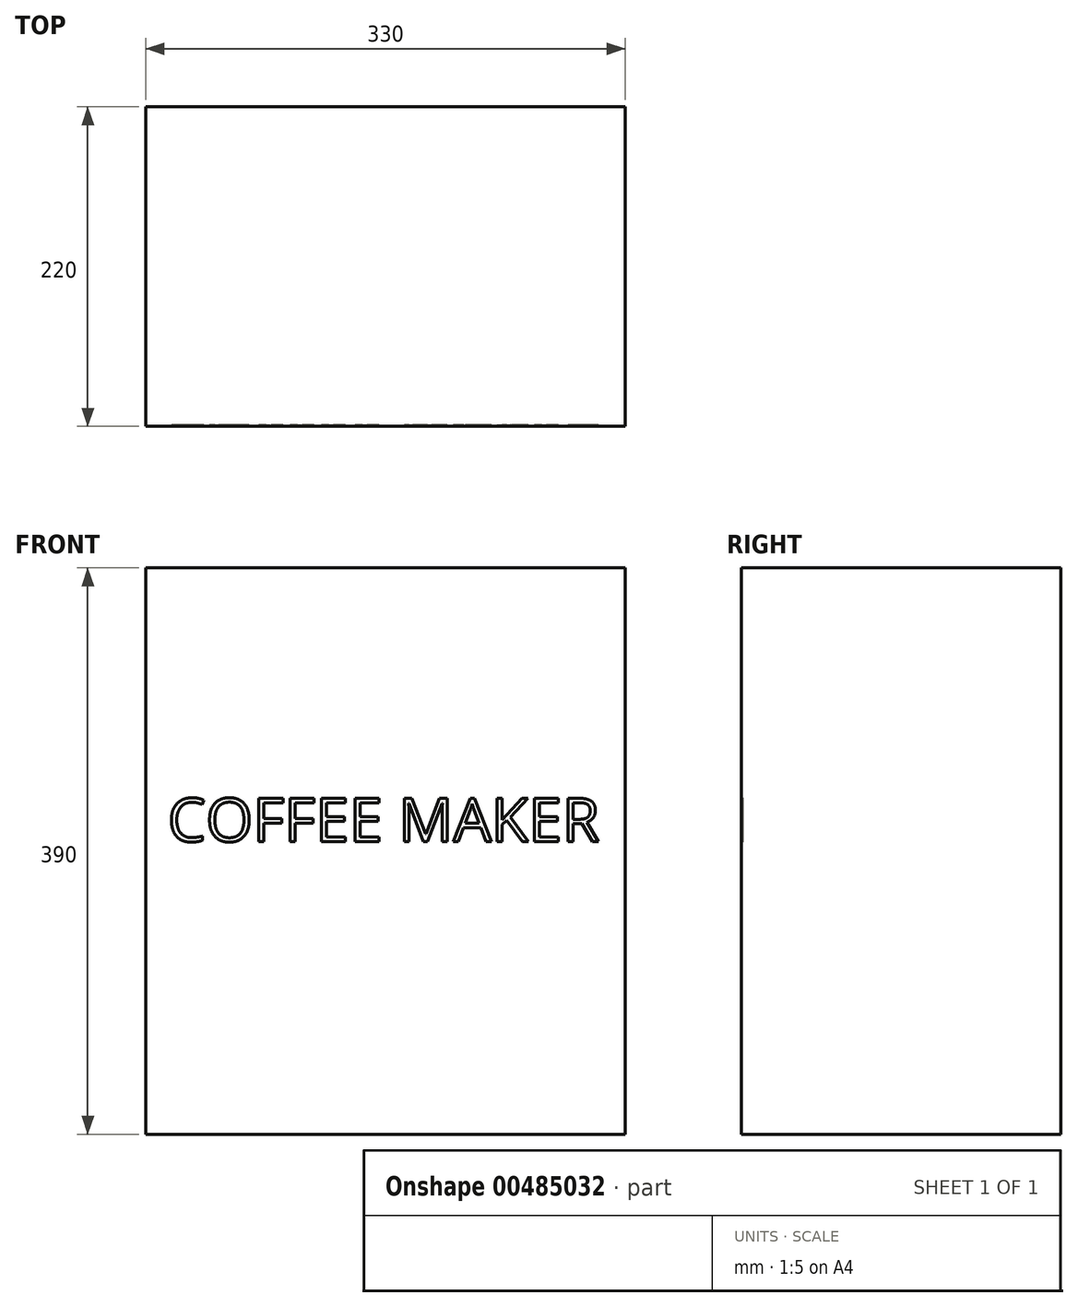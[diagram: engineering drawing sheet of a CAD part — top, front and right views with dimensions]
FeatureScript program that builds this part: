
annotation { "Feature Type Name" : "Feature", "Feature Type Description" : "" }
export const myFeature = defineFeature(function(context is Context, id is Id, definition is map)
    precondition{}
    {
        {
            var Q0;
            Q0=qCreatedBy(makeId("Top.planeOp"),FACE);
            var sketch = newSketch(context, id + "F0", { "sketchPlane" : qUnion([Q0])});
            skLineSegment(sketch, "E0.bottom", {"start": v(165, -110) * mm, "end": v(-165, -110) * mm});
            skLineSegment(sketch, "E0.top", {"start": v(165, 110) * mm, "end": v(-165, 110) * mm});
            skLineSegment(sketch, "E0.left", {"start": v(165, -110) * mm, "end": v(165, 110) * mm});
            skLineSegment(sketch, "E0.right", {"start": v(-165, -110) * mm, "end": v(-165, 110) * mm});
            skPoint(sketch, "E0.middle", {"position": v(0, 0) * mm});
            skSolve(sketch);
        }
        {
            var Q0;
            Q0 = qSketchRegion(id + "F0", true);
            extrude(context, id + "F1", {"entities" : qUnion([Q0]), "depth" : 390 * mm});
        }
        {
            var Q0;
            Q0=makeQuery(id+"F1.opExtrude","SWEPT_FACE",FACE,{"disambiguationData":[OSD([sQuery(id+"F0.wireOp",EDGE,"E0.bottom")])]});
            var sketch = newSketch(context, id + "F2", { "sketchPlane" : qUnion([Q0])});
            skText(sketch, "E1", { "text": "COFFEE MAKER", "fontName": "OpenSans-Regular.ttf"});
            const initialGuessF2  = {"E1": [-0.15, 0.20154, 1, 0, 0.03]};
            skSetInitialGuess(sketch, initialGuessF2);
            skSolve(sketch);
        }
        {
            var Q0;
            Q0 = qSketchRegion(id + "F2", true);
            extrude(context, id + "F3", {"entities" : qUnion([Q0]), "operationType" : NewBodyOperationType.REMOVE, "oppositeDirection" : true, "depth" : 1 * mm});
        }
    });
